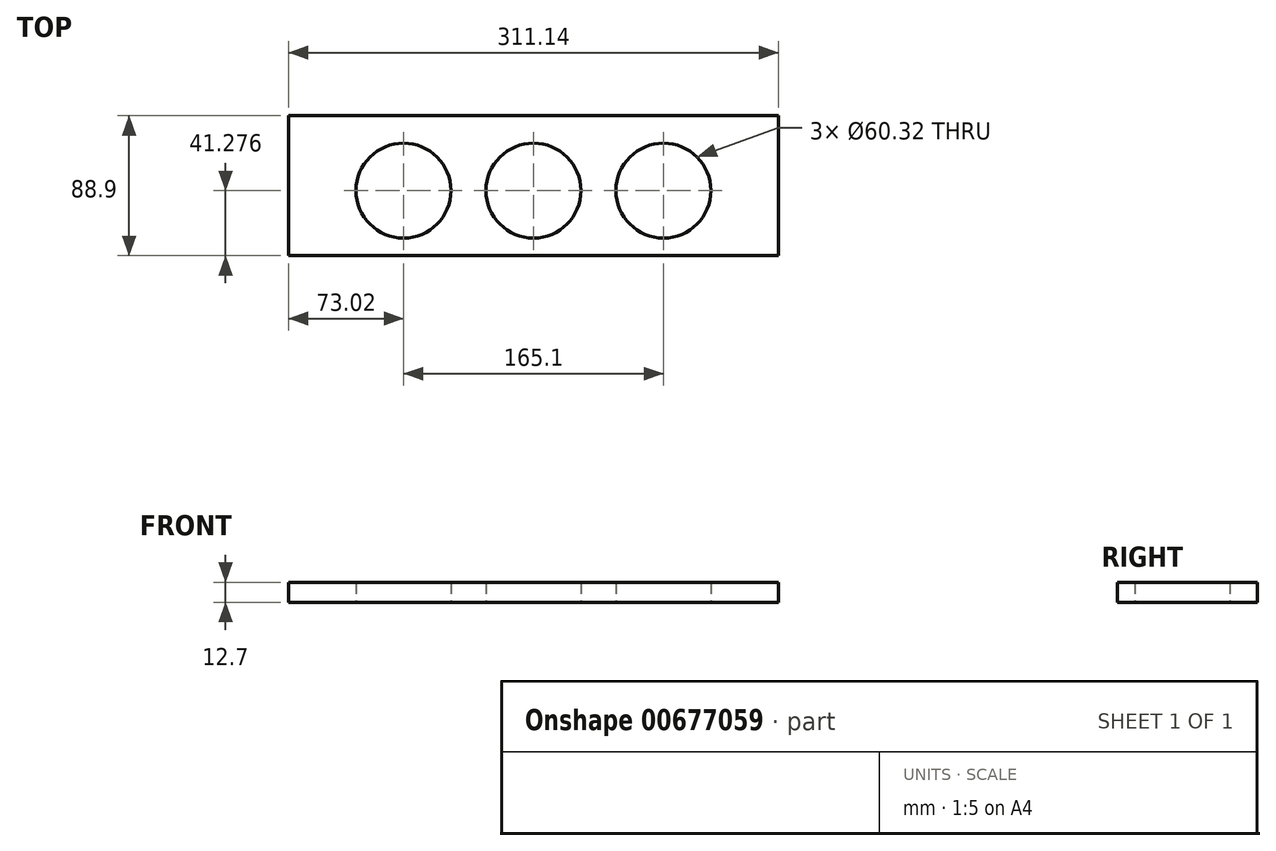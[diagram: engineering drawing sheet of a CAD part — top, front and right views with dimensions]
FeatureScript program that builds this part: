
annotation { "Feature Type Name" : "Feature", "Feature Type Description" : "" }
export const myFeature = defineFeature(function(context is Context, id is Id, definition is map)
    precondition{}
    {
        {
            var Q0;
            Q0=qCreatedBy(makeId("Top.planeOp"),FACE);
            var sketch = newSketch(context, id + "F0", { "sketchPlane" : qUnion([Q0])});
            skLineSegment(sketch, "E0.bottom", {"start": v(-155.58, -4.94) * mm, "end": v(155.58, -4.94) * mm});
            skLineSegment(sketch, "E0.top", {"start": v(-155.58, -93.84) * mm, "end": v(155.58, -93.84) * mm});
            skLineSegment(sketch, "E0.left", {"start": v(-155.58, -4.94) * mm, "end": v(-155.58, -93.84) * mm});
            skLineSegment(sketch, "E0.right", {"start": v(155.58, -4.94) * mm, "end": v(155.58, -93.84) * mm});
            skCircle(sketch, "E1", {"center": v(-82.55, -52.56) * mm, "radius": 30.16 * mm});
            skCircle(sketch, "E2", {"center": v(0, -52.56) * mm, "radius": 30.16 * mm});
            skCircle(sketch, "E3", {"center": v(82.55, -52.56) * mm, "radius": 30.16 * mm});
            skSolve(sketch);
        }
        {
            var Q0;
            Q0=makeQuery(id+"F0.imprint","IMPRINT",FACE,{"disambiguationData":[TD([[makeQuery(id+"F0.imprint","IMPRINT",EDGE,{"derivedFrom":sQuery(id+"F0.wireOp",EDGE,"E0.bottom")}),-1.0]])]});
            extrude(context, id + "F1", {"entities" : qUnion([Q0]), "depth" : 12.7 * mm, "offsetDistance" : 25.4 * mm});
        }
    });
